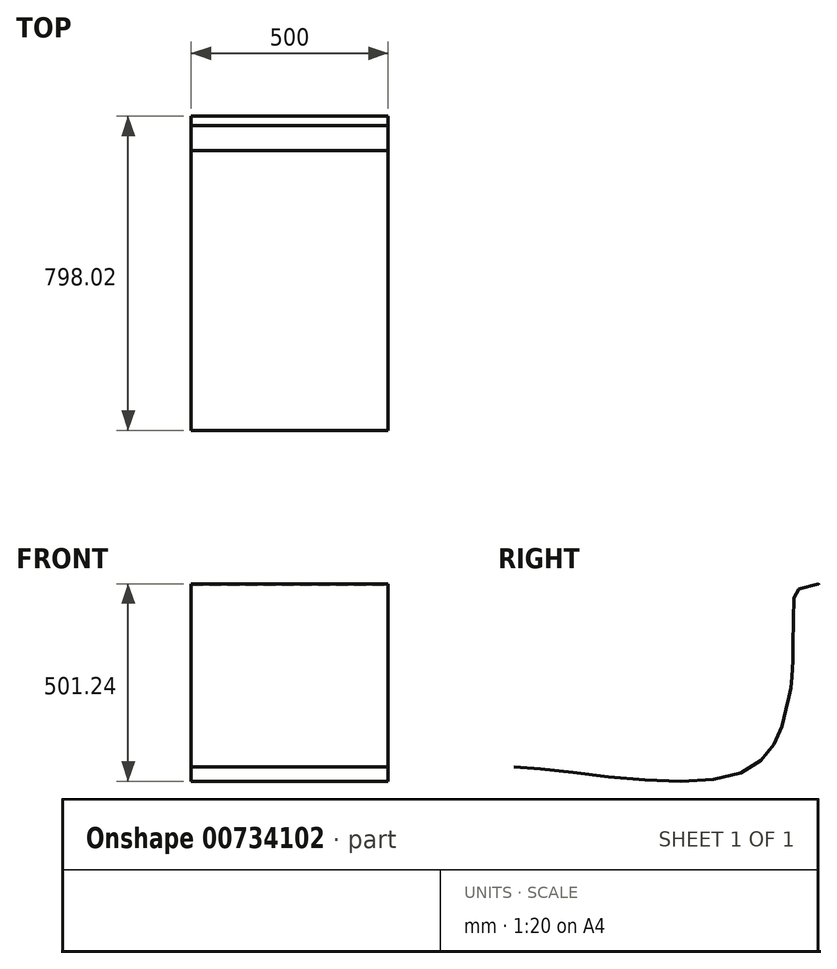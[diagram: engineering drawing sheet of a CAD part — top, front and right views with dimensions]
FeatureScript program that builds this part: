
annotation { "Feature Type Name" : "Feature", "Feature Type Description" : "" }
export const myFeature = defineFeature(function(context is Context, id is Id, definition is map)
    precondition{}
    {
        {
            var Q0;
            Q0=qCreatedBy(makeId("Right.planeOp"),FACE);
            var sketch = newSketch(context, id + "F0", { "sketchPlane" : qUnion([Q0])});
            skFitSpline(sketch, "E0", {"points": [v(-457.84, -143.55) * mm, v(139.43, -148.35) * mm, v(237.77, 23.16) * mm, v(248.57, 85.52) * mm, v(252.16, 247.43) * mm, v(253.36, 270.22) * mm, v(300.14, 320.6) * mm, v(316.93, 319.13) * mm], "startDerivative": vector(1352.25, -38.5) * mm, "endDerivative": vector(-2739.33, -81.13) * mm});
            skSolve(sketch);
        }
        {
            var Q0;
            Q0=sQuery(id+"F0.wireOp",EDGE,"E0");
            extrude(context, id + "F1", {"bodyType" : ToolBodyType.SURFACE, "surfaceEntities" : qUnion([Q0]), "depth" : 500 * mm, "offsetDistance" : 25 * mm});
        }
    });
